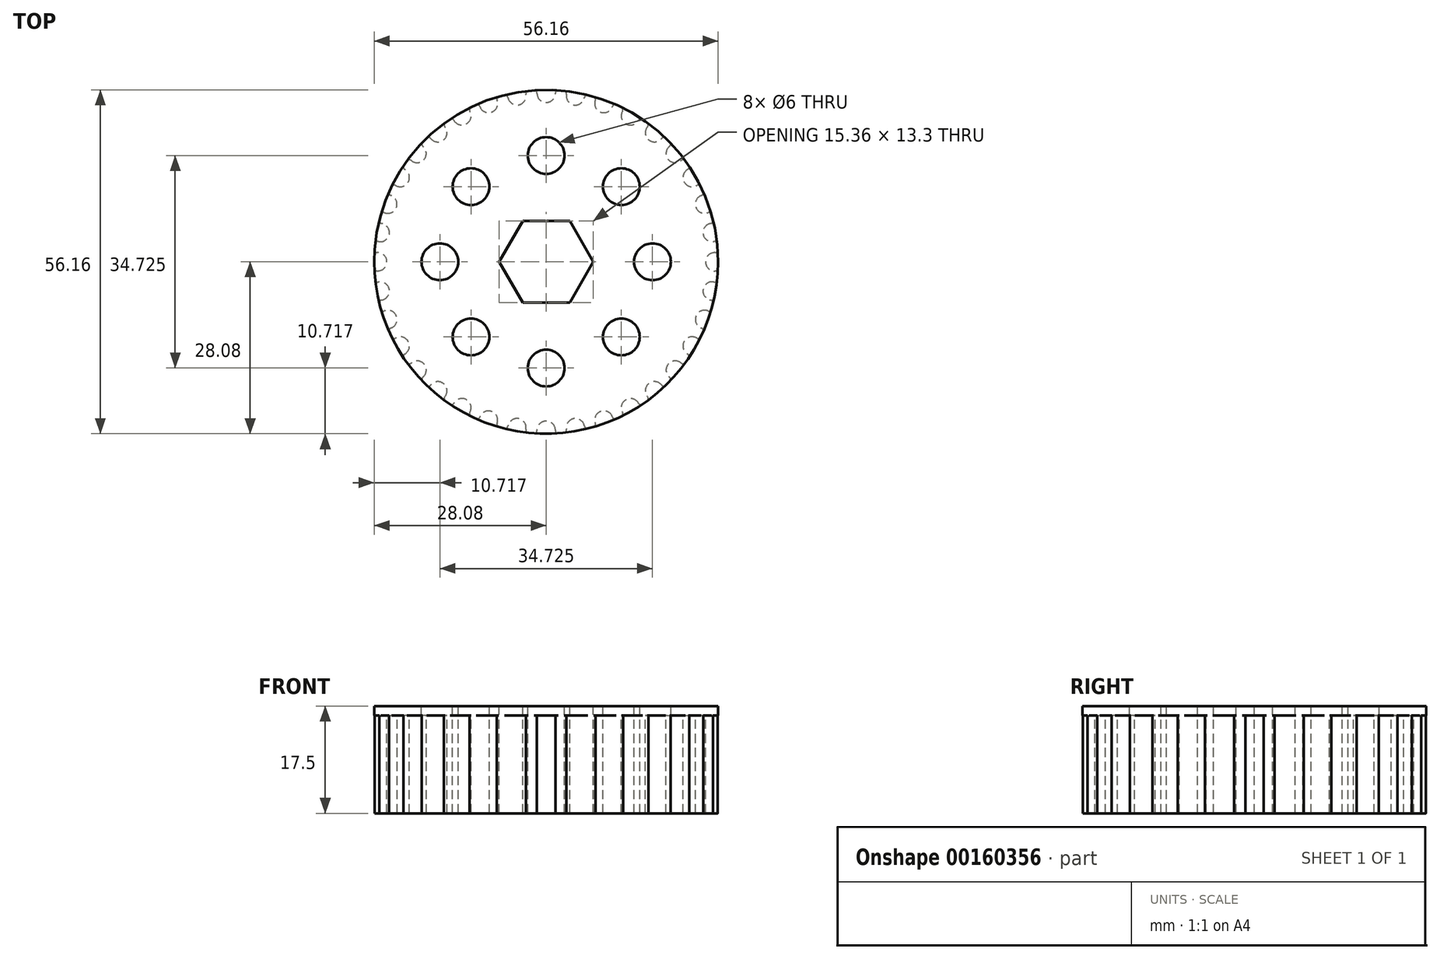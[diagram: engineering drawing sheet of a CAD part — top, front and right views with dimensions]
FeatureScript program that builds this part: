
annotation { "Feature Type Name" : "Feature", "Feature Type Description" : "" }
export const myFeature = defineFeature(function(context is Context, id is Id, definition is map)
    precondition{}
    {
        {
            assignVariable(context, id + "F0", {"name" : "Teeth", "anyValue" : 36});
        }
        {
            assignVariable(context, id + "F1", {"name" : "Width", "anyValue" : 16});
        }
        {
            var Q0;
            Q0=qCreatedBy(makeId("Top.planeOp"),FACE);
            var sketch = newSketch(context, id + "F2", { "sketchPlane" : qUnion([Q0])});
            skCircle(sketch, "E0", {"center": v(0, 0) * mm, "radius": 28.08 * mm});
            skSolve(sketch);
        }
        {
            var Q0;
            Q0=qSketchRegion(id+"F2",true);
            extrude(context, id + "F3", {"entities" : qUnion([Q0]), "depth" : (getVariable(context, 'Width')) * mm});
        }
        {
            var Q0;
            Q0=makeQuery(id+"F3.opExtrude","CAP_FACE",FACE,{"disambiguationData":[OSD([sQuery(id+"F2.wireOp",EDGE,"E0")])],"isStart":false});
            var sketch = newSketch(context, id + "F4", { "sketchPlane" : qUnion([Q0])});
            skCircle(sketch, "E1", {"center": v(0, 0) * mm, "radius": 26.02 * mm, "construction": true});
            skArc(sketch, "E2", {"start": v(-1.5, 27.55) * mm, "mid": v(0, 26.02) * mm, "end": v(1.5, 27.55) * mm});
            skArc(sketch, "E3", {"start": v(1.98, 28) * mm, "mid": v(0, 28.08) * mm, "end": v(-1.98, 28) * mm});
            skArc(sketch, "E4", {"start": v(-1.5, 27.55) * mm, "mid": v(-1.64, 27.88) * mm, "end": v(-1.98, 28) * mm});
            skArc(sketch, "E5", {"start": v(1.98, 28) * mm, "mid": v(1.64, 27.88) * mm, "end": v(1.5, 27.55) * mm});
            skSolve(sketch);
        }
        {
            var Q0;
            Q0=makeQuery(id+"F4.imprint","IMPRINT",FACE,{"disambiguationData":[TD([[makeQuery(id+"F4.imprint","IMPRINT",EDGE,{"derivedFrom":sQuery(id+"F4.wireOp",EDGE,"E2")}),1.0]])]});
            var Q1;
            Q1=makeQuery(id+"F3.opExtrude","CAP_FACE",FACE,{"disambiguationData":[OSD([sQuery(id+"F2.wireOp",EDGE,"E0")])],"isStart":true});
            extrude(context, id + "F5", {"entities" : qUnion([Q0]), "operationType" : NewBodyOperationType.REMOVE, "endBound" : BoundingType.UP_TO_SURFACE, "oppositeDirection" : true, "endBoundEntityFace" : qUnion([Q1]), "depth" : 25 * mm});
        }
        {
            var Q0;
            Q0=makeQuery(id+"F5.boolean.opBoolean","COPY",FACE,{"derivedFrom":makeQuery(id+"F5.opExtrude","SWEPT_FACE",FACE,{"disambiguationData":[OSD([sQuery(id+"F4.wireOp",EDGE,"E4")])]})});
            var Q1;
            Q1=makeQuery(id+"F5.boolean.opBoolean","COPY",FACE,{"derivedFrom":makeQuery(id+"F5.opExtrude","SWEPT_FACE",FACE,{"disambiguationData":[OSD([sQuery(id+"F4.wireOp",EDGE,"kHu0Iwj9-o4Cv-DRlk-4OjM-lw9Y4UkXsprA")])]})});
            var Q2;
            Q2=makeQuery(id+"F5.boolean.opBoolean","COPY",FACE,{"derivedFrom":makeQuery(id+"F5.opExtrude","SWEPT_FACE",FACE,{"disambiguationData":[OSD([sQuery(id+"F4.wireOp",EDGE,"E2")])]})});
            var Q3;
            Q3=makeQuery(id+"F5.boolean.opBoolean","COPY",FACE,{"derivedFrom":makeQuery(id+"F5.opExtrude","SWEPT_FACE",FACE,{"disambiguationData":[OSD([sQuery(id+"F4.wireOp",EDGE,"lCBZwTSR-BtAH-iuKv-YoZ4-wjcx4KIexOll")])]})});
            var Q4;
            Q4=makeQuery(id+"F5.boolean.opBoolean","COPY",FACE,{"derivedFrom":makeQuery(id+"F5.opExtrude","SWEPT_FACE",FACE,{"disambiguationData":[OSD([sQuery(id+"F4.wireOp",EDGE,"E5")])]})});
            var Q5;
            Q5=makeQuery(id+"F3.opExtrude","SWEPT_FACE",FACE,{"disambiguationData":[OSD([sQuery(id+"F2.wireOp",EDGE,"E0")])]});
            circularPattern(context, id + "F6", {"faces" : qUnion([Q0, Q1, Q2, Q3, Q4]), "axis" : qUnion([Q5]), "angle" : 360 * degree, "instanceCount" : getVariable(context, 'Teeth'), "equalSpace" : true, "patternType" : PatternType.FACE});
        }
        {
            var Q0;
            Q0=makeQuery(id+"F3.opExtrude","CAP_FACE",FACE,{"disambiguationData":[OSD([sQuery(id+"F2.wireOp",EDGE,"E0")])],"isStart":false});
            var sketch = newSketch(context, id + "F7", { "sketchPlane" : qUnion([Q0])});
            skCircle(sketch, "E6.0", {"center": v(0, 0) * mm, "radius": 28.08 * mm});
            skSolve(sketch);
        }
        {
            var Q0;
            Q0=qSketchRegion(id+"F7",true);
            extrude(context, id + "F8", {"entities" : qUnion([Q0]), "operationType" : NewBodyOperationType.ADD, "depth" : 1.5 * mm});
        }
        {
            var Q0;
            Q0=makeQuery(id+"F8.opExtrude","CAP_FACE",FACE,{"disambiguationData":[OSD([sQuery(id+"F7.wireOp",EDGE,"E6.0")])],"isStart":false});
            var sketch = newSketch(context, id + "F9", { "sketchPlane" : qUnion([Q0])});
            skCircle(sketch, "E7.cCircle", {"center": v(0, 0) * mm, "radius": 6.65 * mm, "construction": true});
            skLineSegment(sketch, "E7.0", {"start": v(3.84, -6.65) * mm, "end": v(-3.84, -6.65) * mm});
            skLineSegment(sketch, "E7.1", {"start": v(-3.84, -6.65) * mm, "end": v(-7.68, 0) * mm});
            skLineSegment(sketch, "E7.2", {"start": v(-7.68, 0) * mm, "end": v(-3.84, 6.65) * mm});
            skLineSegment(sketch, "E7.3", {"start": v(-3.84, 6.65) * mm, "end": v(3.84, 6.65) * mm});
            skLineSegment(sketch, "E7.4", {"start": v(3.84, 6.65) * mm, "end": v(7.68, 0) * mm});
            skLineSegment(sketch, "E7.5", {"start": v(7.68, 0) * mm, "end": v(3.84, -6.65) * mm});
            skPoint(sketch, "E7.0.midPoint", {"position": v(0, -6.65) * mm});
            skLineSegment(sketch, "E8", {"start": v(7.68, 0) * mm, "end": v(28.08, 0) * mm, "construction": true});
            skPoint(sketch, "E9", {"position": v(17.88, 0) * mm});
            skLineSegment(sketch, "E10", {"start": v(0, -6.65) * mm, "end": v(0, -28.08) * mm, "construction": true});
            skPoint(sketch, "E11", {"position": v(0, -17.36) * mm});
            skCircle(sketch, "E12", {"center": v(0, -17.36) * mm, "radius": 3 * mm});
            skCircle(sketch, "E13.1.0", {"center": v(12.28, -12.28) * mm, "radius": 3 * mm});
            skCircle(sketch, "E13.2.0", {"center": v(17.36, 0) * mm, "radius": 3 * mm});
            skCircle(sketch, "E14.1.3.0", {"center": v(12.28, 12.28) * mm, "radius": 3 * mm});
            skCircle(sketch, "E14.1.4.0", {"center": v(0, 17.36) * mm, "radius": 3 * mm});
            skCircle(sketch, "E14.1.5.0", {"center": v(-12.28, 12.28) * mm, "radius": 3 * mm});
            skCircle(sketch, "E14.1.6.0", {"center": v(-17.36, 0) * mm, "radius": 3 * mm});
            skCircle(sketch, "E14.1.7.0", {"center": v(-12.28, -12.28) * mm, "radius": 3 * mm});
            skSolve(sketch);
        }
        {
            var Q0;
            Q0=makeQuery(id+"F9.imprint","IMPRINT",FACE,{"disambiguationData":[TD([[makeQuery(id+"F9.imprint","IMPRINT",EDGE,{"derivedFrom":sQuery(id+"F9.wireOp",EDGE,"E7.0")}),-1.0]])]});
            var Q1;
            Q1=makeQuery(id+"F9.imprint","IMPRINT",FACE,{"disambiguationData":[TD([[makeQuery(id+"F9.imprint","IMPRINT",EDGE,{"derivedFrom":sQuery(id+"F9.wireOp",EDGE,"E14.1.3.0")}),1.0]])]});
            var Q2;
            Q2=makeQuery(id+"F9.imprint","IMPRINT",FACE,{"disambiguationData":[TD([[makeQuery(id+"F9.imprint","IMPRINT",EDGE,{"derivedFrom":sQuery(id+"F9.wireOp",EDGE,"E13.2.0")}),1.0]])]});
            var Q3;
            Q3=makeQuery(id+"F9.imprint","IMPRINT",FACE,{"disambiguationData":[TD([[makeQuery(id+"F9.imprint","IMPRINT",EDGE,{"derivedFrom":sQuery(id+"F9.wireOp",EDGE,"E13.1.0")}),1.0]])]});
            var Q4;
            Q4=makeQuery(id+"F9.imprint","IMPRINT",FACE,{"disambiguationData":[TD([[makeQuery(id+"F9.imprint","IMPRINT",EDGE,{"derivedFrom":sQuery(id+"F9.wireOp",EDGE,"E12")}),1.0]])]});
            var Q5;
            Q5=makeQuery(id+"F9.imprint","IMPRINT",FACE,{"disambiguationData":[TD([[makeQuery(id+"F9.imprint","IMPRINT",EDGE,{"derivedFrom":sQuery(id+"F9.wireOp",EDGE,"E14.1.7.0")}),1.0]])]});
            var Q6;
            Q6=makeQuery(id+"F9.imprint","IMPRINT",FACE,{"disambiguationData":[TD([[makeQuery(id+"F9.imprint","IMPRINT",EDGE,{"derivedFrom":sQuery(id+"F9.wireOp",EDGE,"E14.1.6.0")}),1.0]])]});
            var Q7;
            Q7=makeQuery(id+"F9.imprint","IMPRINT",FACE,{"disambiguationData":[TD([[makeQuery(id+"F9.imprint","IMPRINT",EDGE,{"derivedFrom":sQuery(id+"F9.wireOp",EDGE,"E14.1.5.0")}),1.0]])]});
            var Q8;
            Q8=makeQuery(id+"F9.imprint","IMPRINT",FACE,{"disambiguationData":[TD([[makeQuery(id+"F9.imprint","IMPRINT",EDGE,{"derivedFrom":sQuery(id+"F9.wireOp",EDGE,"E14.1.4.0")}),1.0]])]});
            extrude(context, id + "F10", {"entities" : qUnion([Q0, Q1, Q2, Q3, Q4, Q5, Q6, Q7, Q8]), "operationType" : NewBodyOperationType.REMOVE, "endBound" : BoundingType.THROUGH_ALL, "oppositeDirection" : true, "depth" : 25 * mm, "offsetDistance" : 25 * mm});
        }
    });
